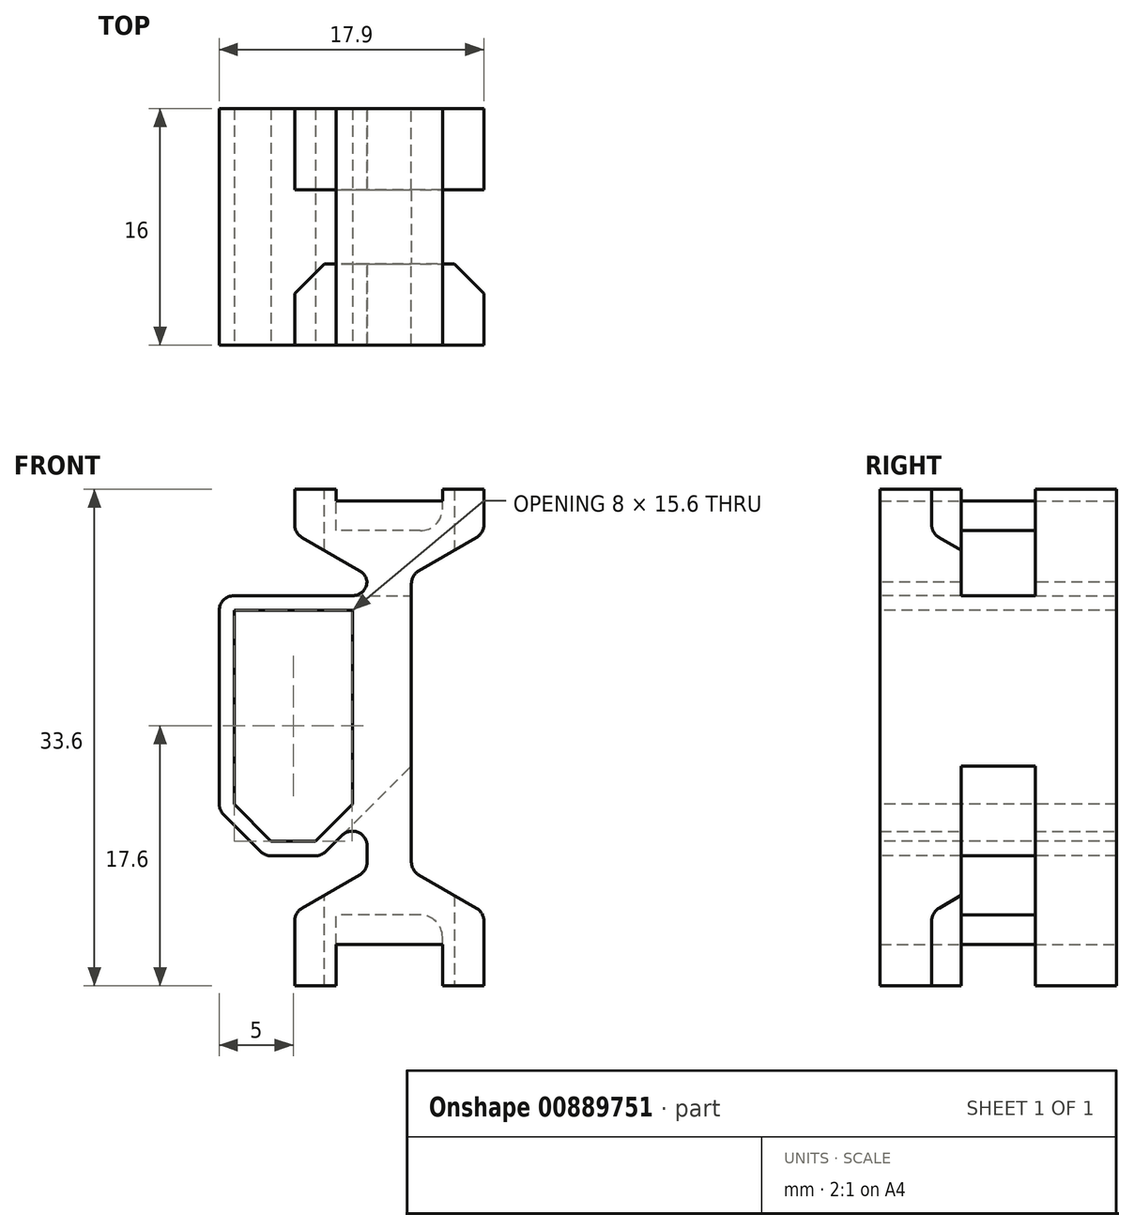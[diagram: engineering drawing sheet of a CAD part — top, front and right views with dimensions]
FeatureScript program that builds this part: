
annotation { "Feature Type Name" : "Feature", "Feature Type Description" : "" }
export const myFeature = defineFeature(function(context is Context, id is Id, definition is map)
    precondition{}
    {
        {
            var Q0;
            Q0=qCreatedBy(makeId("Front.planeOp"),FACE);
            var sketch = newSketch(context, id + "F0", { "sketchPlane" : qUnion([Q0])});
            skLineSegment(sketch, "E0.bottom", {"start": v(-6.4, 30.8) * mm, "end": v(-3.6, 30.8) * mm});
            skLineSegment(sketch, "E0.top", {"start": v(-6.4, -2.8) * mm, "end": v(-3.6, -2.8) * mm});
            skLineSegment(sketch, "E0.left", {"start": v(-6.4, 30.8) * mm, "end": v(-6.4, 27.83) * mm});
            skLineSegment(sketch, "E0.right", {"start": v(-3.6, 30.8) * mm, "end": v(-3.6, 30) * mm});
            skLineSegment(sketch, "E1.bottom", {"start": v(3.6, 30.8) * mm, "end": v(6.4, 30.8) * mm});
            skLineSegment(sketch, "E1.top", {"start": v(3.6, -2.8) * mm, "end": v(6.4, -2.8) * mm});
            skLineSegment(sketch, "E1.left", {"start": v(3.6, 30.8) * mm, "end": v(3.6, 30) * mm});
            skLineSegment(sketch, "E1.right", {"start": v(6.4, 30.8) * mm, "end": v(6.4, 27.83) * mm});
            skLineSegment(sketch, "E2.bottom", {"start": v(-3.6, 0) * mm, "end": v(3.6, 0) * mm});
            skLineSegment(sketch, "E2.top", {"start": v(-3.6, 30) * mm, "end": v(3.6, 30) * mm});
            skPoint(sketch, "E3", {"position": v(-5, 30.8) * mm});
            skPoint(sketch, "E4", {"position": v(5, 30.8) * mm});
            skLineSegment(sketch, "E5.trimOffspring", {"start": v(-6.4, 2.17) * mm, "end": v(-6.4, -2.8) * mm});
            skLineSegment(sketch, "E6.trimOffspring", {"start": v(-3.6, 0) * mm, "end": v(-3.6, -2.8) * mm});
            skLineSegment(sketch, "E7.trimOffspring", {"start": v(3.6, 0) * mm, "end": v(3.6, -2.8) * mm});
            skLineSegment(sketch, "E8", {"start": v(0, 30) * mm, "end": v(0, 0) * mm, "construction": true});
            skLineSegment(sketch, "E9", {"start": v(6.4, 15) * mm, "end": v(0, 15) * mm, "construction": true});
            skLineSegment(sketch, "E10", {"start": v(-6.4, 27.83) * mm, "end": v(-1.5, 25) * mm});
            skLineSegment(sketch, "E11", {"start": v(-1.5, 25) * mm, "end": v(-1.5, 5) * mm});
            skLineSegment(sketch, "E12", {"start": v(-1.5, 5) * mm, "end": v(-6.4, 2.17) * mm});
            skLineSegment(sketch, "E13.MirrorCS", {"start": v(1.5, 5) * mm, "end": v(6.4, 2.17) * mm});
            skLineSegment(sketch, "E14.MirrorCS", {"start": v(6.4, 27.83) * mm, "end": v(1.5, 25) * mm});
            skLineSegment(sketch, "E15.MirrorCS", {"start": v(1.5, 25) * mm, "end": v(1.5, 5) * mm});
            skLineSegment(sketch, "E16.trimOffspring", {"start": v(6.4, 2.17) * mm, "end": v(6.4, -2.8) * mm});
            skSolve(sketch);
        }
        {
            var Q0;
            Q0=qSketchRegion(id+"F0",true);
            extrude(context, id + "F1", {"entities" : qUnion([Q0]), "depth" : 16 * mm});
        }
        {
            var Q0;
            Q0=makeQuery(id+"F1.opExtrude","SWEPT_FACE",FACE,{"disambiguationData":[OSD([sQuery(id+"F0.wireOp",EDGE,"E0.bottom")])]});
            var sketch = newSketch(context, id + "F2", { "sketchPlane" : qUnion([Q0])});
            skLineSegment(sketch, "E17", {"start": v(-6.4, -8) * mm, "end": v(6.4, -8) * mm, "construction": true});
            skLineSegment(sketch, "E18.0.1", {"start": v(-6.4, -5.5) * mm, "end": v(-6.4, -10.5) * mm});
            skLineSegment(sketch, "E18.0.3", {"start": v(-3.6, -10.5) * mm, "end": v(-3.6, -5.5) * mm});
            skLineSegment(sketch, "E19.0.1", {"start": v(3.6, -5.5) * mm, "end": v(3.6, -10.5) * mm});
            skLineSegment(sketch, "E19.0.3", {"start": v(6.4, -10.5) * mm, "end": v(6.4, -5.5) * mm});
            skLineSegment(sketch, "E20", {"start": v(-6.4, -5.5) * mm, "end": v(-3.6, -5.5) * mm});
            skLineSegment(sketch, "E21.MirrorCS", {"start": v(-6.4, -10.5) * mm, "end": v(-3.6, -10.5) * mm});
            skLineSegment(sketch, "E22.trimOffspring", {"start": v(3.6, -5.5) * mm, "end": v(6.4, -5.5) * mm});
            skLineSegment(sketch, "E23.trimOffspring", {"start": v(3.6, -10.5) * mm, "end": v(6.4, -10.5) * mm});
            skSolve(sketch);
        }
        {
            var Q0;
            Q0=makeQuery(id+"F2.imprint","IMPRINT",FACE,{"disambiguationData":[TD([[makeQuery(id+"F2.imprint","IMPRINT",EDGE,{"derivedFrom":sQuery(id+"F2.wireOp",EDGE,"E18.0.1")}),-1.0]])]});
            var Q1;
            Q1=makeQuery(id+"F2.imprint","IMPRINT",FACE,{"disambiguationData":[TD([[makeQuery(id+"F2.imprint","IMPRINT",EDGE,{"derivedFrom":sQuery(id+"F2.wireOp",EDGE,"E19.0.1")}),1.0]])]});
            extrude(context, id + "F3", {"entities" : qUnion([Q0, Q1]), "operationType" : NewBodyOperationType.REMOVE, "endBound" : BoundingType.THROUGH_ALL, "oppositeDirection" : true, "depth" : 25 * mm});
        }
        {
            var Q0;
            Q0=makeQuery(id+"F3.boolean.opBoolean","COPY",FACE,{"disambiguationData":[TD([makeQuery(id+"F1.opExtrude","SWEPT_FACE",FACE,{"disambiguationData":[OSD([sQuery(id+"F0.wireOp",EDGE,"E2.bottom")])]})])],"derivedFrom":makeQuery(id+"F3.opExtrude","SWEPT_FACE",FACE,{"disambiguationData":[OSD([sQuery(id+"F2.wireOp",EDGE,"E18.0.3")])]})});
            var sketch = newSketch(context, id + "F4", { "sketchPlane" : qUnion([Q0])});
            skLineSegment(sketch, "E24.bottom", {"start": v(5.5, 2) * mm, "end": v(10.5, 2) * mm});
            skLineSegment(sketch, "E24.top", {"start": v(5.5, 28) * mm, "end": v(10.5, 28) * mm});
            skLineSegment(sketch, "E24.left", {"start": v(5.5, 2) * mm, "end": v(5.5, 28) * mm});
            skLineSegment(sketch, "E24.right", {"start": v(10.5, 2) * mm, "end": v(10.5, 28) * mm});
            skSolve(sketch);
        }
        {
            var Q0;
            Q0=qSketchRegion(id+"F4",true);
            extrude(context, id + "F5", {"entities" : qUnion([Q0]), "operationType" : NewBodyOperationType.REMOVE, "endBound" : BoundingType.THROUGH_ALL, "oppositeDirection" : true, "depth" : 25 * mm});
        }
        {
            var Q0;
            Q0=makeQuery(id+"F1.opExtrude","CAP_FACE",FACE,{"disambiguationData":[OSD([sQuery(id+"F0.wireOp",EDGE,"E0.bottom"),sQuery(id+"F0.wireOp",EDGE,"E0.top"),sQuery(id+"F0.wireOp",EDGE,"E0.left"),sQuery(id+"F0.wireOp",EDGE,"E0.right"),sQuery(id+"F0.wireOp",EDGE,"E1.bottom"),sQuery(id+"F0.wireOp",EDGE,"E1.top"),sQuery(id+"F0.wireOp",EDGE,"E1.left"),sQuery(id+"F0.wireOp",EDGE,"E1.right"),sQuery(id+"F0.wireOp",EDGE,"E2.bottom"),sQuery(id+"F0.wireOp",EDGE,"E2.top"),sQuery(id+"F0.wireOp",EDGE,"E5.trimOffspring"),sQuery(id+"F0.wireOp",EDGE,"E6.trimOffspring"),sQuery(id+"F0.wireOp",EDGE,"E7.trimOffspring"),sQuery(id+"F0.wireOp",EDGE,"XNyugLao-tsnu-Sah3-VUFn-nM4j8uXXMLVh"),sQuery(id+"F0.wireOp",EDGE,"qag7rgW7-rpCx-CGtA-zPlC-gOamsbcd0Z1q"),sQuery(id+"F0.wireOp",EDGE,"LMqOLITl-EVo5-MTzV-QNNo-kao2bXQrC091"),sQuery(id+"F0.wireOp",EDGE,"kiGqG5in-MVmp-Csza-V1P0-bwSz3CtIkC7l")])],"isStart":false});
            var sketch = newSketch(context, id + "F6", { "sketchPlane" : qUnion([Q0])});
            skLineSegment(sketch, "E25", {"start": v(-10.5, 22.6) * mm, "end": v(-10.5, 9.5) * mm});
            skLineSegment(sketch, "E26", {"start": v(-10.5, 9.5) * mm, "end": v(-8, 7) * mm});
            skLineSegment(sketch, "E27", {"start": v(-8, 7) * mm, "end": v(-5, 7) * mm});
            skLineSegment(sketch, "E28", {"start": v(-6.5, 7) * mm, "end": v(-6.5, 22.6) * mm, "construction": true});
            skLineSegment(sketch, "E29.0", {"start": v(-4.59, 6) * mm, "end": v(1.5, 12.09) * mm});
            skLineSegment(sketch, "E29.1", {"start": v(-11.5, 23.6) * mm, "end": v(-11.5, 23.6) * mm});
            skLineSegment(sketch, "E29.2", {"start": v(-11.5, 23.6) * mm, "end": v(-11.5, 9.09) * mm});
            skLineSegment(sketch, "E29.3", {"start": v(-11.5, 9.09) * mm, "end": v(-8.41, 6) * mm});
            skLineSegment(sketch, "E29.4", {"start": v(-8.41, 6) * mm, "end": v(-4.59, 6) * mm});
            skLineSegment(sketch, "E30", {"start": v(-11.5, 23.6) * mm, "end": v(1.5, 23.6) * mm});
            skLineSegment(sketch, "E31", {"start": v(1.5, 12.09) * mm, "end": v(1.5, 23.6) * mm});
            skLineSegment(sketch, "E32.MirrorCS", {"start": v(-2.5, 9.5) * mm, "end": v(-5, 7) * mm});
            skLineSegment(sketch, "E33.MirrorCS", {"start": v(-2.5, 22.6) * mm, "end": v(-2.5, 9.5) * mm});
            skLineSegment(sketch, "E34", {"start": v(-10.5, 22.6) * mm, "end": v(-2.5, 22.6) * mm});
            skSolve(sketch);
        }
        {
            var Q0;
            Q0=qSketchRegion(id+"F6",true);
            var Q1;
            Q1=makeQuery(id+"F1.opExtrude","CAP_FACE",FACE,{"disambiguationData":[OSD([sQuery(id+"F0.wireOp",EDGE,"E0.bottom"),sQuery(id+"F0.wireOp",EDGE,"E0.top"),sQuery(id+"F0.wireOp",EDGE,"E0.left"),sQuery(id+"F0.wireOp",EDGE,"E0.right"),sQuery(id+"F0.wireOp",EDGE,"E1.bottom"),sQuery(id+"F0.wireOp",EDGE,"E1.top"),sQuery(id+"F0.wireOp",EDGE,"E1.left"),sQuery(id+"F0.wireOp",EDGE,"E1.right"),sQuery(id+"F0.wireOp",EDGE,"E2.bottom"),sQuery(id+"F0.wireOp",EDGE,"E2.top"),sQuery(id+"F0.wireOp",EDGE,"E5.trimOffspring"),sQuery(id+"F0.wireOp",EDGE,"E6.trimOffspring"),sQuery(id+"F0.wireOp",EDGE,"E7.trimOffspring"),sQuery(id+"F0.wireOp",EDGE,"XNyugLao-tsnu-Sah3-VUFn-nM4j8uXXMLVh"),sQuery(id+"F0.wireOp",EDGE,"qag7rgW7-rpCx-CGtA-zPlC-gOamsbcd0Z1q"),sQuery(id+"F0.wireOp",EDGE,"LMqOLITl-EVo5-MTzV-QNNo-kao2bXQrC091"),sQuery(id+"F0.wireOp",EDGE,"kiGqG5in-MVmp-Csza-V1P0-bwSz3CtIkC7l")])],"isStart":true});
            extrude(context, id + "F7", {"entities" : qUnion([Q0]), "operationType" : NewBodyOperationType.ADD, "endBound" : BoundingType.UP_TO_SURFACE, "oppositeDirection" : true, "endBoundEntityFace" : qUnion([Q1]), "depth" : 25 * mm});
        }
        {
            var Q0;
            Q0=makeQuery(id+"F5.boolean.opBoolean","INTERSECT",EDGE,{"derivedFrom":[makeQuery(id+"F3.boolean.opBoolean","COPY",FACE,{"disambiguationData":[TD([makeQuery(id+"F1.opExtrude","SWEPT_FACE",FACE,{"disambiguationData":[OSD([sQuery(id+"F0.wireOp",EDGE,"E2.bottom")])]})])],"derivedFrom":makeQuery(id+"F3.opExtrude","SWEPT_FACE",FACE,{"disambiguationData":[OSD([sQuery(id+"F2.wireOp",EDGE,"E19.0.1")])]})}),makeQuery(id+"F5.opExtrude","SWEPT_FACE",FACE,{"disambiguationData":[OSD([sQuery(id+"F4.wireOp",EDGE,"E24.bottom")])]})]});
            var Q1;
            Q1=makeQuery(id+"F5.boolean.opBoolean","INTERSECT",EDGE,{"derivedFrom":[makeQuery(id+"F3.boolean.opBoolean","COPY",FACE,{"disambiguationData":[TD([makeQuery(id+"F1.opExtrude","SWEPT_FACE",FACE,{"disambiguationData":[OSD([sQuery(id+"F0.wireOp",EDGE,"E1.left")])]})])],"derivedFrom":makeQuery(id+"F3.opExtrude","SWEPT_FACE",FACE,{"disambiguationData":[OSD([sQuery(id+"F2.wireOp",EDGE,"E19.0.1")])]})}),makeQuery(id+"F5.opExtrude","SWEPT_FACE",FACE,{"disambiguationData":[OSD([sQuery(id+"F4.wireOp",EDGE,"E24.top")])]})]});
            var Q2;
            Q2=makeQuery(id+"F5.boolean.opBoolean","COPY",EDGE,{"derivedFrom":makeQuery(id+"F5.opExtrude","CAP_EDGE",EDGE,{"disambiguationData":[OSD([sQuery(id+"F4.wireOp",EDGE,"E24.top")])],"isStart":true})});
            var Q3;
            Q3=makeQuery(id+"F5.boolean.opBoolean","COPY",EDGE,{"derivedFrom":makeQuery(id+"F5.opExtrude","CAP_EDGE",EDGE,{"disambiguationData":[OSD([sQuery(id+"F4.wireOp",EDGE,"E24.bottom")])],"isStart":true})});
            fillet(context, id + "F8", {"entities" : qUnion([Q0, Q1, Q2, Q3]), "radius" : 1.5 * mm, "tangentPropagation" : true, "allowEdgeOverflow" : false});
        }
        {
            var Q0;
            {var subQ0=sQuery(id+"F2.wireOp",EDGE,"E23.trimOffspring");Q0=makeQuery(id+"F3.boolean.opBoolean","COPY",EDGE,{"disambiguationData":[TD([makeQuery(id+"F1.opExtrude","SWEPT_FACE",FACE,{"disambiguationData":[OSD([sQuery(id+"F0.wireOp",EDGE,"E1.top")])]})])],"derivedFrom":makeQuery(id+"F3.opExtrude","SWEPT_EDGE",EDGE,{"disambiguationData":[OSD([sQuery(id+"F2.wireOp",EDGE,"E19.0.3"),subQ0])]})});}
            var Q1;
            {var subQ0=sQuery(id+"F2.wireOp",EDGE,"E22.trimOffspring");Q1=makeQuery(id+"F3.boolean.opBoolean","COPY",EDGE,{"disambiguationData":[TD([makeQuery(id+"F1.opExtrude","SWEPT_FACE",FACE,{"disambiguationData":[OSD([sQuery(id+"F0.wireOp",EDGE,"E1.top")])]})])],"derivedFrom":makeQuery(id+"F3.opExtrude","SWEPT_EDGE",EDGE,{"disambiguationData":[OSD([sQuery(id+"F2.wireOp",EDGE,"E19.0.3"),subQ0])]})});}
            var Q2;
            {var subQ0=sQuery(id+"F2.wireOp",EDGE,"E23.trimOffspring");Q2=makeQuery(id+"F3.boolean.opBoolean","COPY",EDGE,{"disambiguationData":[TD([makeQuery(id+"F1.opExtrude","SWEPT_FACE",FACE,{"disambiguationData":[OSD([sQuery(id+"F0.wireOp",EDGE,"E1.bottom")])]})])],"derivedFrom":makeQuery(id+"F3.opExtrude","SWEPT_EDGE",EDGE,{"disambiguationData":[OSD([sQuery(id+"F2.wireOp",EDGE,"E19.0.3"),subQ0])]})});}
            var Q3;
            {var subQ0=sQuery(id+"F2.wireOp",EDGE,"E22.trimOffspring");Q3=makeQuery(id+"F3.boolean.opBoolean","COPY",EDGE,{"disambiguationData":[TD([makeQuery(id+"F1.opExtrude","SWEPT_FACE",FACE,{"disambiguationData":[OSD([sQuery(id+"F0.wireOp",EDGE,"E1.bottom")])]})])],"derivedFrom":makeQuery(id+"F3.opExtrude","SWEPT_EDGE",EDGE,{"disambiguationData":[OSD([sQuery(id+"F2.wireOp",EDGE,"E19.0.3"),subQ0])]})});}
            var Q4;
            {var subQ0=sQuery(id+"F2.wireOp",EDGE,"E20");Q4=makeQuery(id+"F3.boolean.opBoolean","COPY",EDGE,{"disambiguationData":[TD([makeQuery(id+"F1.opExtrude","SWEPT_FACE",FACE,{"disambiguationData":[OSD([sQuery(id+"F0.wireOp",EDGE,"E0.top")])]})])],"derivedFrom":makeQuery(id+"F3.opExtrude","SWEPT_EDGE",EDGE,{"disambiguationData":[OSD([sQuery(id+"F0.wireOp",EDGE,"E0.bottom"),sQuery(id+"F0.wireOp",EDGE,"E0.left"),sQuery(id+"F2.wireOp",EDGE,"E18.0.1"),subQ0])]})});}
            var Q5;
            {var subQ0=sQuery(id+"F2.wireOp",EDGE,"E21.MirrorCS");Q5=makeQuery(id+"F3.boolean.opBoolean","COPY",EDGE,{"disambiguationData":[TD([makeQuery(id+"F1.opExtrude","SWEPT_FACE",FACE,{"disambiguationData":[OSD([sQuery(id+"F0.wireOp",EDGE,"E0.top")])]})])],"derivedFrom":makeQuery(id+"F3.opExtrude","SWEPT_EDGE",EDGE,{"disambiguationData":[OSD([sQuery(id+"F0.wireOp",EDGE,"E0.bottom"),sQuery(id+"F0.wireOp",EDGE,"E0.left"),sQuery(id+"F2.wireOp",EDGE,"E18.0.1"),subQ0])]})});}
            var Q6;
            {var subQ0=sQuery(id+"F0.wireOp",EDGE,"E0.bottom");var subQ1=sQuery(id+"F2.wireOp",EDGE,"E20");var subQ2=sQuery(id+"F0.wireOp",EDGE,"E0.left");Q6=makeQuery(id+"F3.boolean.opBoolean","COPY",EDGE,{"disambiguationData":[TD([makeQuery(id+"F1.opExtrude","SWEPT_FACE",FACE,{"disambiguationData":[OSD([subQ0])]})])],"derivedFrom":makeQuery(id+"F3.opExtrude","SWEPT_EDGE",EDGE,{"disambiguationData":[OSD([subQ0,subQ2,sQuery(id+"F2.wireOp",EDGE,"E18.0.1"),subQ1])]})});}
            var Q7;
            {var subQ0=sQuery(id+"F0.wireOp",EDGE,"E0.bottom");var subQ1=sQuery(id+"F2.wireOp",EDGE,"E21.MirrorCS");var subQ2=sQuery(id+"F0.wireOp",EDGE,"E0.left");Q7=makeQuery(id+"F3.boolean.opBoolean","COPY",EDGE,{"disambiguationData":[TD([makeQuery(id+"F1.opExtrude","SWEPT_FACE",FACE,{"disambiguationData":[OSD([subQ0])]})])],"derivedFrom":makeQuery(id+"F3.opExtrude","SWEPT_EDGE",EDGE,{"disambiguationData":[OSD([subQ0,subQ2,sQuery(id+"F2.wireOp",EDGE,"E18.0.1"),subQ1])]})});}
            chamfer(context, id + "F9", {"entities" : qUnion([Q0, Q1, Q2, Q3, Q4, Q5, Q6, Q7]), "width" : 2 * mm, "tangentPropagation" : true});
        }
        {
            var Q0;
            Q0=makeQuery(id+"F7.opExtrude","SWEPT_EDGE",EDGE,{"disambiguationData":[OSD([sQuery(id+"F6.wireOp",EDGE,"E29.2"),sQuery(id+"F6.wireOp",EDGE,"E30")])]});
            var Q1;
            Q1=makeQuery(id+"F7.opExtrude","SWEPT_EDGE",EDGE,{"disambiguationData":[OSD([sQuery(id+"F6.wireOp",EDGE,"E29.2"),sQuery(id+"F6.wireOp",EDGE,"E29.3")])]});
            var Q2;
            Q2=makeQuery(id+"F7.opExtrude","SWEPT_EDGE",EDGE,{"disambiguationData":[OSD([sQuery(id+"F6.wireOp",EDGE,"E29.3"),sQuery(id+"F6.wireOp",EDGE,"E29.4")])]});
            var Q3;
            Q3=makeQuery(id+"F7.opExtrude","SWEPT_EDGE",EDGE,{"disambiguationData":[OSD([sQuery(id+"F6.wireOp",EDGE,"E29.0"),sQuery(id+"F6.wireOp",EDGE,"E29.4")])]});
            var Q4;
            {var subQ19=sQuery(id+"F0.wireOp",EDGE,"E11");Q4=makeQuery(id+"F7.boolean.opBoolean","INTERSECT",EDGE,{"derivedFrom":[makeQuery(id+"F5.boolean.opBoolean","SPLIT",FACE,{"disambiguationData":[TD([makeQuery(id+"F5.opExtrude","SWEPT_FACE",FACE,{"disambiguationData":[OSD([sQuery(id+"F4.wireOp",EDGE,"E24.right")])]})])],"derivedFrom":makeQuery(id+"F1.opExtrude","SWEPT_FACE",FACE,{"disambiguationData":[OSD([subQ19])]})}),makeQuery(id+"F7.opExtrude","SWEPT_FACE",FACE,{"disambiguationData":[OSD([sQuery(id+"F6.wireOp",EDGE,"E29.0")])]})]});}
            var Q5;
            {var subQ20=sQuery(id+"F0.wireOp",EDGE,"E11");Q5=makeQuery(id+"F7.boolean.opBoolean","INTERSECT",EDGE,{"derivedFrom":[makeQuery(id+"F5.boolean.opBoolean","SPLIT",FACE,{"disambiguationData":[TD([makeQuery(id+"F5.opExtrude","SWEPT_FACE",FACE,{"disambiguationData":[OSD([sQuery(id+"F4.wireOp",EDGE,"E24.left")])]})])],"derivedFrom":makeQuery(id+"F1.opExtrude","SWEPT_FACE",FACE,{"disambiguationData":[OSD([subQ20])]})}),makeQuery(id+"F7.opExtrude","SWEPT_FACE",FACE,{"disambiguationData":[OSD([sQuery(id+"F6.wireOp",EDGE,"E29.0")])]})]});}
            var Q6;
            {var subQ19=sQuery(id+"F0.wireOp",EDGE,"E11");Q6=makeQuery(id+"F7.boolean.opBoolean","INTERSECT",EDGE,{"derivedFrom":[makeQuery(id+"F5.boolean.opBoolean","SPLIT",FACE,{"disambiguationData":[TD([makeQuery(id+"F5.opExtrude","SWEPT_FACE",FACE,{"disambiguationData":[OSD([sQuery(id+"F4.wireOp",EDGE,"E24.right")])]})])],"derivedFrom":makeQuery(id+"F1.opExtrude","SWEPT_FACE",FACE,{"disambiguationData":[OSD([subQ19])]})}),makeQuery(id+"F7.opExtrude","SWEPT_FACE",FACE,{"disambiguationData":[OSD([sQuery(id+"F6.wireOp",EDGE,"E30")])]})]});}
            var Q7;
            {var subQ20=sQuery(id+"F0.wireOp",EDGE,"E11");Q7=makeQuery(id+"F7.boolean.opBoolean","INTERSECT",EDGE,{"derivedFrom":[makeQuery(id+"F5.boolean.opBoolean","SPLIT",FACE,{"disambiguationData":[TD([makeQuery(id+"F5.opExtrude","SWEPT_FACE",FACE,{"disambiguationData":[OSD([sQuery(id+"F4.wireOp",EDGE,"E24.left")])]})])],"derivedFrom":makeQuery(id+"F1.opExtrude","SWEPT_FACE",FACE,{"disambiguationData":[OSD([subQ20])]})}),makeQuery(id+"F7.opExtrude","SWEPT_FACE",FACE,{"disambiguationData":[OSD([sQuery(id+"F6.wireOp",EDGE,"E30")])]})]});}
            var Q8;
            {var subQ0=sQuery(id+"F0.wireOp",EDGE,"E12");var subQ1=sQuery(id+"F0.wireOp",EDGE,"E5.trimOffspring");Q8=makeQuery(id+"F3.boolean.opBoolean","SPLIT",EDGE,{"disambiguationData":[TD([makeQuery(id+"F3.opExtrude","SWEPT_FACE",FACE,{"disambiguationData":[OSD([sQuery(id+"F2.wireOp",EDGE,"E21.MirrorCS")])]})])],"derivedFrom":makeQuery(id+"F1.opExtrude","SWEPT_EDGE",EDGE,{"disambiguationData":[OSD([subQ1,subQ0])]})});}
            var Q9;
            {var subQ0=sQuery(id+"F0.wireOp",EDGE,"E12");var subQ1=sQuery(id+"F0.wireOp",EDGE,"E5.trimOffspring");Q9=makeQuery(id+"F3.boolean.opBoolean","SPLIT",EDGE,{"disambiguationData":[TD([makeQuery(id+"F3.opExtrude","SWEPT_FACE",FACE,{"disambiguationData":[OSD([sQuery(id+"F2.wireOp",EDGE,"E20")])]})])],"derivedFrom":makeQuery(id+"F1.opExtrude","SWEPT_EDGE",EDGE,{"disambiguationData":[OSD([subQ1,subQ0])]})});}
            var Q10;
            {var subQ0=sQuery(id+"F0.wireOp",EDGE,"E10");var subQ1=sQuery(id+"F0.wireOp",EDGE,"E0.left");Q10=makeQuery(id+"F3.boolean.opBoolean","SPLIT",EDGE,{"disambiguationData":[TD([makeQuery(id+"F3.opExtrude","SWEPT_FACE",FACE,{"disambiguationData":[OSD([sQuery(id+"F2.wireOp",EDGE,"E21.MirrorCS")])]})])],"derivedFrom":makeQuery(id+"F1.opExtrude","SWEPT_EDGE",EDGE,{"disambiguationData":[OSD([subQ1,subQ0])]})});}
            var Q11;
            {var subQ0=sQuery(id+"F0.wireOp",EDGE,"E10");var subQ1=sQuery(id+"F0.wireOp",EDGE,"E0.left");Q11=makeQuery(id+"F3.boolean.opBoolean","SPLIT",EDGE,{"disambiguationData":[TD([makeQuery(id+"F3.opExtrude","SWEPT_FACE",FACE,{"disambiguationData":[OSD([sQuery(id+"F2.wireOp",EDGE,"E20")])]})])],"derivedFrom":makeQuery(id+"F1.opExtrude","SWEPT_EDGE",EDGE,{"disambiguationData":[OSD([subQ1,subQ0])]})});}
            var Q12;
            {var subQ0=sQuery(id+"F0.wireOp",EDGE,"E14.MirrorCS");var subQ1=sQuery(id+"F0.wireOp",EDGE,"E1.right");Q12=makeQuery(id+"F3.boolean.opBoolean","SPLIT",EDGE,{"disambiguationData":[TD([makeQuery(id+"F3.opExtrude","SWEPT_FACE",FACE,{"disambiguationData":[OSD([sQuery(id+"F2.wireOp",EDGE,"E23.trimOffspring")])]})])],"derivedFrom":makeQuery(id+"F1.opExtrude","SWEPT_EDGE",EDGE,{"disambiguationData":[OSD([subQ1,subQ0])]})});}
            var Q13;
            {var subQ0=sQuery(id+"F0.wireOp",EDGE,"E14.MirrorCS");var subQ1=sQuery(id+"F0.wireOp",EDGE,"E1.right");Q13=makeQuery(id+"F3.boolean.opBoolean","SPLIT",EDGE,{"disambiguationData":[TD([makeQuery(id+"F3.opExtrude","SWEPT_FACE",FACE,{"disambiguationData":[OSD([sQuery(id+"F2.wireOp",EDGE,"E22.trimOffspring")])]})])],"derivedFrom":makeQuery(id+"F1.opExtrude","SWEPT_EDGE",EDGE,{"disambiguationData":[OSD([subQ1,subQ0])]})});}
            var Q14;
            {var subQ0=sQuery(id+"F0.wireOp",EDGE,"E16.trimOffspring");var subQ1=sQuery(id+"F0.wireOp",EDGE,"E13.MirrorCS");Q14=makeQuery(id+"F3.boolean.opBoolean","SPLIT",EDGE,{"disambiguationData":[TD([makeQuery(id+"F3.opExtrude","SWEPT_FACE",FACE,{"disambiguationData":[OSD([sQuery(id+"F2.wireOp",EDGE,"E23.trimOffspring")])]})])],"derivedFrom":makeQuery(id+"F1.opExtrude","SWEPT_EDGE",EDGE,{"disambiguationData":[OSD([subQ1,subQ0])]})});}
            var Q15;
            {var subQ0=sQuery(id+"F0.wireOp",EDGE,"E16.trimOffspring");var subQ1=sQuery(id+"F0.wireOp",EDGE,"E13.MirrorCS");Q15=makeQuery(id+"F3.boolean.opBoolean","SPLIT",EDGE,{"disambiguationData":[TD([makeQuery(id+"F3.opExtrude","SWEPT_FACE",FACE,{"disambiguationData":[OSD([sQuery(id+"F2.wireOp",EDGE,"E22.trimOffspring")])]})])],"derivedFrom":makeQuery(id+"F1.opExtrude","SWEPT_EDGE",EDGE,{"disambiguationData":[OSD([subQ1,subQ0])]})});}
            var Q16;
            {var subQ8=sQuery(id+"F0.wireOp",EDGE,"E15.MirrorCS");var subQ9=sQuery(id+"F0.wireOp",EDGE,"E13.MirrorCS");Q16=makeQuery(id+"F5.boolean.opBoolean","SPLIT",EDGE,{"disambiguationData":[TD([makeQuery(id+"F5.opExtrude","SWEPT_FACE",FACE,{"disambiguationData":[OSD([sQuery(id+"F4.wireOp",EDGE,"E24.right")])]})])],"derivedFrom":makeQuery(id+"F1.opExtrude","SWEPT_EDGE",EDGE,{"disambiguationData":[OSD([subQ9,subQ8])]})});}
            var Q17;
            {var subQ8=sQuery(id+"F0.wireOp",EDGE,"E15.MirrorCS");var subQ11=sQuery(id+"F0.wireOp",EDGE,"E13.MirrorCS");Q17=makeQuery(id+"F5.boolean.opBoolean","SPLIT",EDGE,{"disambiguationData":[TD([makeQuery(id+"F5.opExtrude","SWEPT_FACE",FACE,{"disambiguationData":[OSD([sQuery(id+"F4.wireOp",EDGE,"E24.left")])]})])],"derivedFrom":makeQuery(id+"F1.opExtrude","SWEPT_EDGE",EDGE,{"disambiguationData":[OSD([subQ11,subQ8])]})});}
            var Q18;
            {var subQ8=sQuery(id+"F0.wireOp",EDGE,"E15.MirrorCS");var subQ10=sQuery(id+"F0.wireOp",EDGE,"E14.MirrorCS");Q18=makeQuery(id+"F5.boolean.opBoolean","SPLIT",EDGE,{"disambiguationData":[TD([makeQuery(id+"F5.opExtrude","SWEPT_FACE",FACE,{"disambiguationData":[OSD([sQuery(id+"F4.wireOp",EDGE,"E24.left")])]})])],"derivedFrom":makeQuery(id+"F1.opExtrude","SWEPT_EDGE",EDGE,{"disambiguationData":[OSD([subQ10,subQ8])]})});}
            var Q19;
            {var subQ8=sQuery(id+"F0.wireOp",EDGE,"E15.MirrorCS");var subQ9=sQuery(id+"F0.wireOp",EDGE,"E14.MirrorCS");Q19=makeQuery(id+"F5.boolean.opBoolean","SPLIT",EDGE,{"disambiguationData":[TD([makeQuery(id+"F5.opExtrude","SWEPT_FACE",FACE,{"disambiguationData":[OSD([sQuery(id+"F4.wireOp",EDGE,"E24.right")])]})])],"derivedFrom":makeQuery(id+"F1.opExtrude","SWEPT_EDGE",EDGE,{"disambiguationData":[OSD([subQ9,subQ8])]})});}
            var Q20;
            {var subQ8=sQuery(id+"F0.wireOp",EDGE,"E12");var subQ18=sQuery(id+"F0.wireOp",EDGE,"E11");Q20=makeQuery(id+"F5.boolean.opBoolean","SPLIT",EDGE,{"disambiguationData":[TD([makeQuery(id+"F5.opExtrude","SWEPT_FACE",FACE,{"disambiguationData":[OSD([sQuery(id+"F4.wireOp",EDGE,"E24.left")])]})])],"derivedFrom":makeQuery(id+"F1.opExtrude","SWEPT_EDGE",EDGE,{"disambiguationData":[OSD([subQ18,subQ8])]})});}
            var Q21;
            {var subQ8=sQuery(id+"F0.wireOp",EDGE,"E11");var subQ17=sQuery(id+"F0.wireOp",EDGE,"E12");Q21=makeQuery(id+"F5.boolean.opBoolean","SPLIT",EDGE,{"disambiguationData":[TD([makeQuery(id+"F5.opExtrude","SWEPT_FACE",FACE,{"disambiguationData":[OSD([sQuery(id+"F4.wireOp",EDGE,"E24.right")])]})])],"derivedFrom":makeQuery(id+"F1.opExtrude","SWEPT_EDGE",EDGE,{"disambiguationData":[OSD([subQ8,subQ17])]})});}
            var Q22;
            {var subQ5=sQuery(id+"F0.wireOp",EDGE,"E10");var subQ9=sQuery(id+"F0.wireOp",EDGE,"E11");Q22=makeQuery(id+"F5.boolean.opBoolean","SPLIT",EDGE,{"disambiguationData":[TD([makeQuery(id+"F5.opExtrude","SWEPT_FACE",FACE,{"disambiguationData":[OSD([sQuery(id+"F4.wireOp",EDGE,"E24.right")])]})])],"derivedFrom":makeQuery(id+"F1.opExtrude","SWEPT_EDGE",EDGE,{"disambiguationData":[OSD([subQ5,subQ9])]})});}
            var Q23;
            {var subQ5=sQuery(id+"F0.wireOp",EDGE,"E10");var subQ9=sQuery(id+"F0.wireOp",EDGE,"E11");Q23=makeQuery(id+"F5.boolean.opBoolean","SPLIT",EDGE,{"disambiguationData":[TD([makeQuery(id+"F5.opExtrude","SWEPT_FACE",FACE,{"disambiguationData":[OSD([sQuery(id+"F4.wireOp",EDGE,"E24.left")])]})])],"derivedFrom":makeQuery(id+"F1.opExtrude","SWEPT_EDGE",EDGE,{"disambiguationData":[OSD([subQ5,subQ9])]})});}
            fillet(context, id + "F10", {"entities" : qUnion([Q0, Q1, Q2, Q3, Q4, Q5, Q6, Q7, Q8, Q9, Q10, Q11, Q12, Q13, Q14, Q15, Q16, Q17, Q18, Q19, Q20, Q21, Q22, Q23]), "radius" : 1 * mm, "tangentPropagation" : true, "allowEdgeOverflow" : false});
        }
    });
